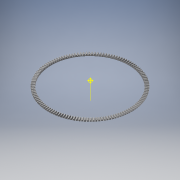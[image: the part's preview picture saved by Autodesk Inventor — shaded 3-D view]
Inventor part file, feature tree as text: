
AUTODESK INVENTOR PART (.ipt)
format: ipt  version: 2017 (Build 210142000, 142)  size: 1,877,504 bytes
history: native  units: mm
features: other x24, loft x2, pattern_circular x2, sketch x2, extrude x1
ambient origin geometry x6: Origin, XZ Plane, X Axis, Y Axis, Z Axis, Center Point
bodies: Solid1 (feature_tree)
feature tree (31):
  other  "Top Point"
  other  "Mesh Plane2"
  other  "Teeth Body"
  other  "Start Point"
  other  "Tooth Plane"
  other  "Start Sketch"
  other  "End Point"
  other  "3D Sketch Right"
  other  "End Plane Right"
  loft  "Loft Right"
  pattern_circular  "Circular Pattern Right"  [2 undecoded]
  other  "3D Sketch Left"
  other  "End Plane Left"
  loft  "Loft Left"
  pattern_circular  "Circular Pattern Left"  Angle=90.0deg  [1 undecoded]
  other  "Fix Body"
  extrude  "Extrusion1"  Depth=10.0mm
  other  "Mesh Plane"
  other  "Top Plane"
  other  "Teeth Body Sketch"
  other  "End Plane"
  other  "End Sketch"
  other  "Helical Curve Left"
  other  "End Sketch Left"
  other  "Body Sketch"
  sketch  "Sketch6"  dims[d0=330.2mm d1=329.501251mm]
  other  "Srf1"
  other  "Helical Curve Right"
  other  "End Sketch Right"
  sketch  "Sketch8"  dims[d2=330.78229mm d3=12.7mm d4=16.526741mm d5=90.0deg d7=493.522657mm d8=468.312989mm d9=1278.766519mm d11=12.9794mm d12=455.473429mm d15=432.207357mm d16=1180.177168mm d17=0.0mm d18=90.0deg d19=0.0mm d20=90.0deg d21=1300.0mm d22=360.0deg d26=408.108671mm d27=1.487752mm d28=330.2mm d29=-14.559197mm d30=455.473429mm d31=432.207357mm d32=1180.177168mm d35=0.0mm d37=0.0mm d39=0.0mm d40=90.0deg d41=1300.0mm d42=360.0deg d46=90.0deg d47=90.0deg d48=0.0mm d49=0.0mm d50=90.0deg d51=0.241661mm d52=0.0mm d53=0.0mm d54=0.0mm d56=17.556067mm d57=1444.576572mm d58=1436.641612mm d59=1333.203726mm d60=1325.880529mm d61=1333.203726mm d62=1325.880529mm d63=90.0deg d64=90.0deg d65=408.108671mm d66=31.5mm d67=330.2mm d68=-14.559197mm d69=1.487752mm d70=432.207357mm d71=1180.177168mm d72=455.473429mm d73=1325.880529mm d74=1333.203726mm d75=0.0mm d76=90.0deg d77=0.0mm d78=90.0deg d79=0.0mm d80=90.0deg d81=1300.0mm d82=360.0deg d84=10.0mm d85=20.0mm d86=20.0mm d87=10.0mm d88=0.0mm d89=0.0mm d90=304.8mm d91=25.4mm d92=0.0mm]
  other  "Pitch Diameter"
note: 3 required parameter values undecoded (feature->parameter linkage not recoverable at this tier; creation-order binding heuristic only, values carry confidence <= 0.55)
